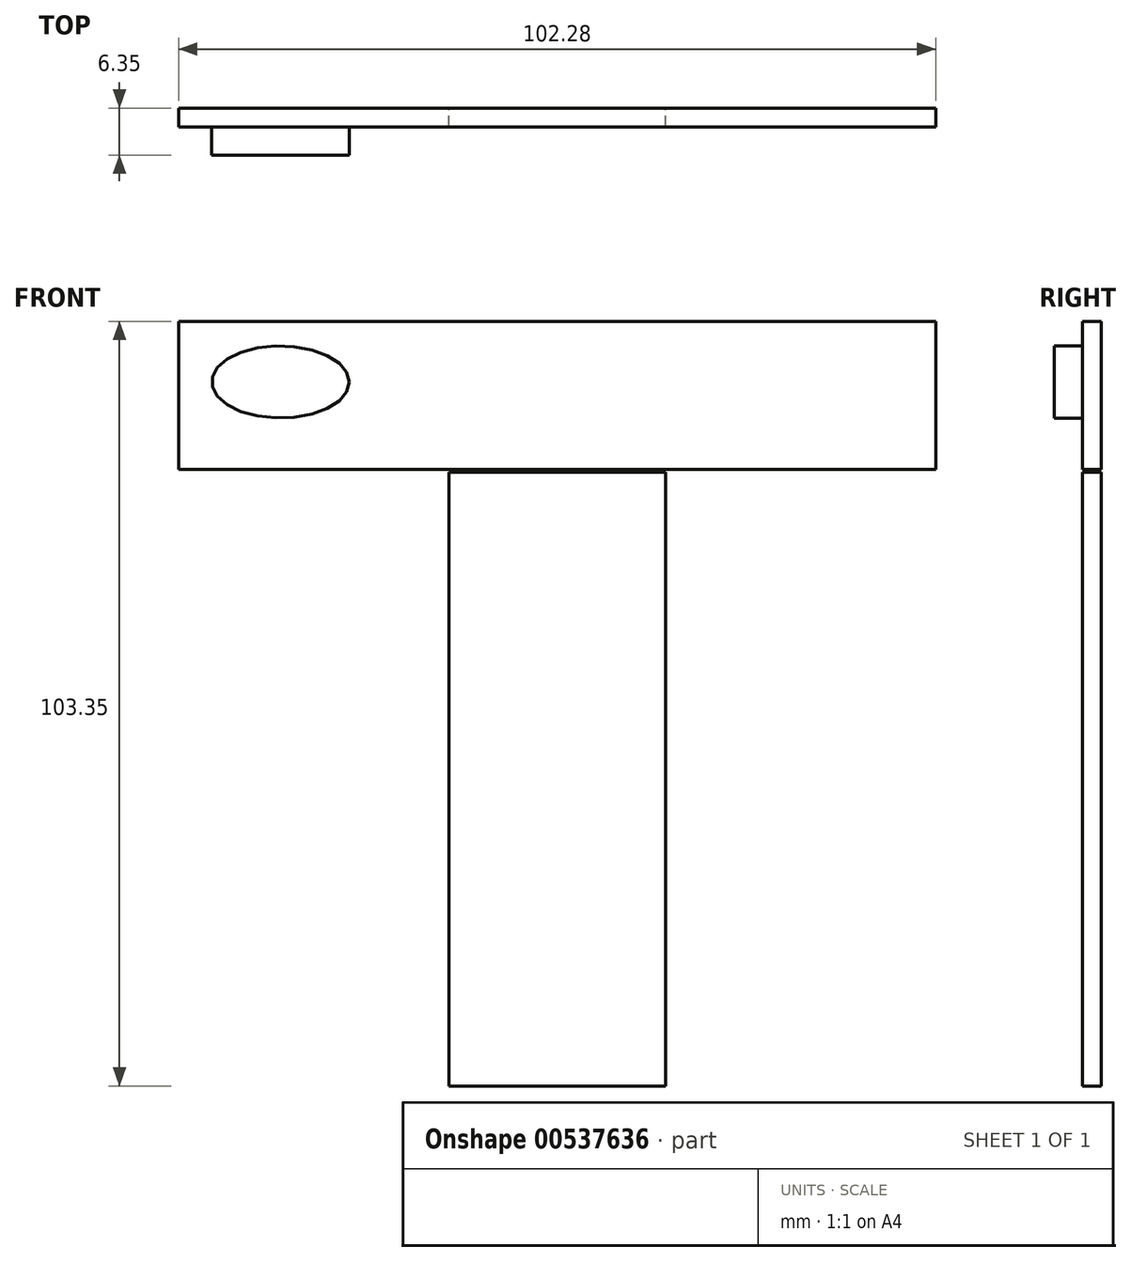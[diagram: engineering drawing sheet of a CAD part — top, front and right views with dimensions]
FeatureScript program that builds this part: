
annotation { "Feature Type Name" : "Feature", "Feature Type Description" : "" }
export const myFeature = defineFeature(function(context is Context, id is Id, definition is map)
    precondition{}
    {
        {
            var Q0;
            Q0=qCreatedBy(makeId("Front.planeOp"),FACE);
            var sketch = newSketch(context, id + "F0", { "sketchPlane" : qUnion([Q0])});
            skLineSegment(sketch, "E0.bottom", {"start": v(-51.14, 41.88) * mm, "end": v(51.14, 41.88) * mm});
            skLineSegment(sketch, "E0.top", {"start": v(-51.14, 61.86) * mm, "end": v(51.14, 61.86) * mm});
            skLineSegment(sketch, "E0.left", {"start": v(-51.14, 41.88) * mm, "end": v(-51.14, 61.86) * mm});
            skLineSegment(sketch, "E0.right", {"start": v(51.14, 41.88) * mm, "end": v(51.14, 61.86) * mm});
            skPoint(sketch, "E0.middle", {"position": v(0, 51.87) * mm});
            skLineSegment(sketch, "E1.bottom", {"start": v(-14.62, -41.5) * mm, "end": v(14.62, -41.5) * mm});
            skLineSegment(sketch, "E1.top", {"start": v(-14.62, 41.5) * mm, "end": v(14.62, 41.5) * mm});
            skLineSegment(sketch, "E1.left", {"start": v(-14.62, -41.5) * mm, "end": v(-14.62, 41.5) * mm});
            skLineSegment(sketch, "E1.right", {"start": v(14.62, -41.5) * mm, "end": v(14.62, 41.5) * mm});
            skPoint(sketch, "E1.middle", {"position": v(0, 0) * mm});
            skSolve(sketch);
        }
        {
            var Q0;
            Q0=qCreatedBy(makeId("Front.planeOp"),FACE);
            var sketch = newSketch(context, id + "F1", { "sketchPlane" : qUnion([Q0])});
            skEllipse(sketch, "E2", {"center": v(-37.4, 53.68) * mm, "majorRadius": 9.3 * mm, "minorRadius": 4.88 * mm, "majorAxis": v(1, 0)});
            skSolve(sketch);
        }
        {
            var Q0;
            Q0=makeQuery(id+"F0.imprint","IMPRINT",FACE,{"disambiguationData":[TD([[makeQuery(id+"F0.imprint","IMPRINT",EDGE,{"derivedFrom":sQuery(id+"F0.wireOp",EDGE,"E0.bottom")}),1.0]])]});
            var Q1;
            Q1 = qSketchRegion(id + "F0", true);
            extrude(context, id + "F2", {"entities" : qUnion([Q0, Q1]), "depth" : 2.54 * mm, "offsetDistance" : 25.4 * mm});
        }
        {
            var Q0;
            Q0 = qSketchRegion(id + "F1", true);
            extrude(context, id + "F3", {"entities" : qUnion([Q0]), "operationType" : NewBodyOperationType.ADD, "depth" : 6.35 * mm, "offsetDistance" : 25.4 * mm});
        }
    });
